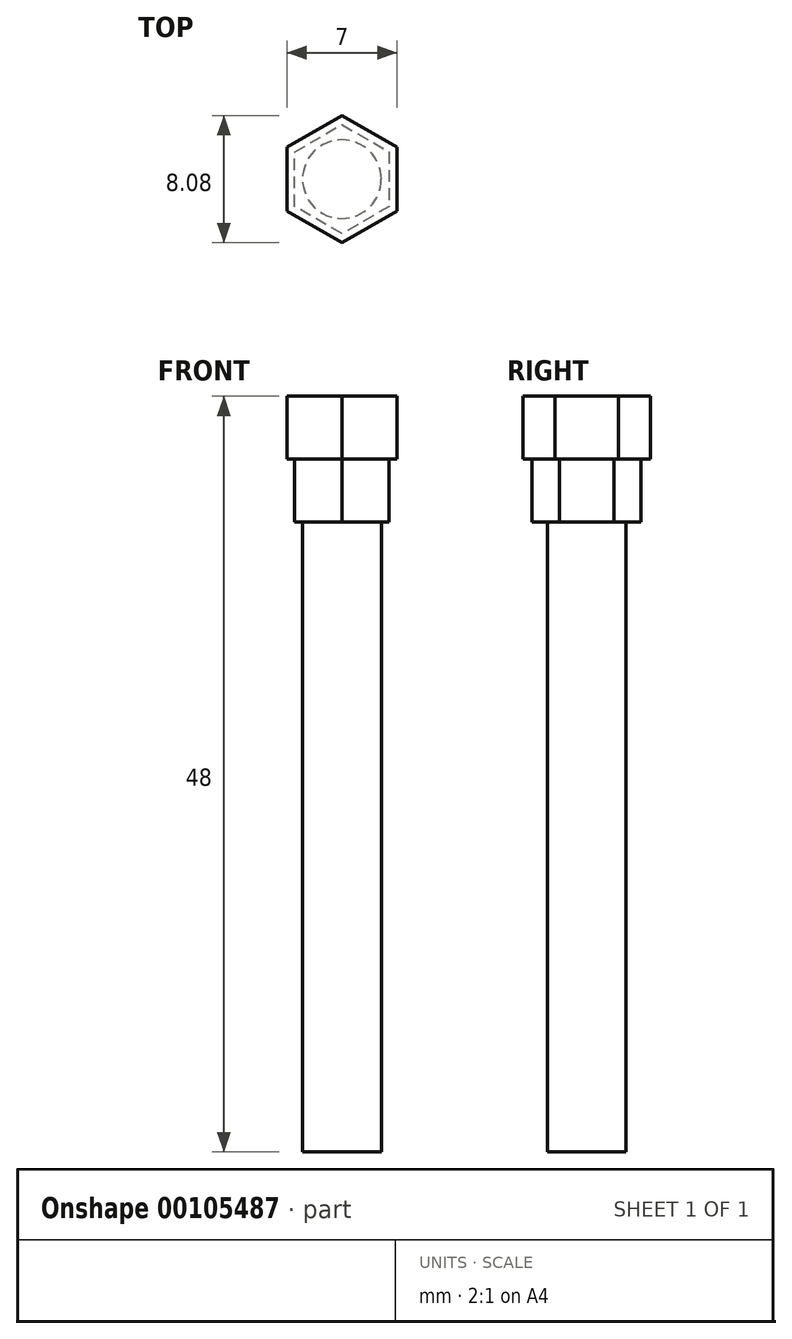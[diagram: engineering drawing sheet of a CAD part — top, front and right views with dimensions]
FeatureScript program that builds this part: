
annotation { "Feature Type Name" : "Feature", "Feature Type Description" : "" }
export const myFeature = defineFeature(function(context is Context, id is Id, definition is map)
    precondition{}
    {
        {
            var Q0;
            Q0=qCreatedBy(makeId("Top.planeOp"),FACE);
            var sketch = newSketch(context, id + "F0", { "sketchPlane" : qUnion([Q0])});
            skCircle(sketch, "E0", {"center": v(0, 0) * mm, "radius": 2.5 * mm});
            skSolve(sketch);
        }
        {
            var Q0;
            Q0=makeQuery(id+"F0.imprint","IMPRINT",FACE,{"disambiguationData":[TD([[makeQuery(id+"F0.imprint","IMPRINT",EDGE,{"derivedFrom":sQuery(id+"F0.wireOp",EDGE,"E0")}),1.0]])]});
            extrude(context, id + "F1", {"entities" : qUnion([Q0]), "depth" : 40 * mm});
        }
        {
            var Q0;
            Q0=makeQuery(id+"F1.opExtrude","CAP_FACE",FACE,{"disambiguationData":[OSD([sQuery(id+"F0.wireOp",EDGE,"E0")])],"isStart":false});
            var sketch = newSketch(context, id + "F2", { "sketchPlane" : qUnion([Q0])});
            skCircle(sketch, "E1.cCircle", {"center": v(0, 0) * mm, "radius": 3 * mm, "construction": true});
            skLineSegment(sketch, "E1.0", {"start": v(3, 1.73) * mm, "end": v(3, -1.73) * mm});
            skLineSegment(sketch, "E1.1", {"start": v(3, -1.73) * mm, "end": v(0, -3.46) * mm});
            skLineSegment(sketch, "E1.2", {"start": v(0, -3.46) * mm, "end": v(-3, -1.73) * mm});
            skLineSegment(sketch, "E1.3", {"start": v(-3, -1.73) * mm, "end": v(-3, 1.73) * mm});
            skLineSegment(sketch, "E1.4", {"start": v(-3, 1.73) * mm, "end": v(0, 3.46) * mm});
            skLineSegment(sketch, "E1.5", {"start": v(0, 3.46) * mm, "end": v(3, 1.73) * mm});
            skPoint(sketch, "E1.0.midPoint", {"position": v(3, 0) * mm});
            skSolve(sketch);
        }
        {
            var Q0;
            Q0=qSketchRegion(id+"F2",true);
            extrude(context, id + "F3", {"entities" : qUnion([Q0]), "operationType" : NewBodyOperationType.ADD, "depth" : 4 * mm});
        }
        {
            var Q0;
            Q0=makeQuery(id+"F3.opExtrude","CAP_FACE",FACE,{"disambiguationData":[OSD([sQuery(id+"F2.wireOp",EDGE,"E1.0"),sQuery(id+"F2.wireOp",EDGE,"E1.1"),sQuery(id+"F2.wireOp",EDGE,"E1.2"),sQuery(id+"F2.wireOp",EDGE,"E1.3"),sQuery(id+"F2.wireOp",EDGE,"E1.4"),sQuery(id+"F2.wireOp",EDGE,"E1.5")])],"isStart":false});
            var sketch = newSketch(context, id + "F4", { "sketchPlane" : qUnion([Q0])});
            skCircle(sketch, "E2.cCircle", {"center": v(0, 0) * mm, "radius": 3.5 * mm, "construction": true});
            skLineSegment(sketch, "E2.0", {"start": v(3.5, 2.02) * mm, "end": v(3.5, -2.02) * mm});
            skLineSegment(sketch, "E2.1", {"start": v(3.5, -2.02) * mm, "end": v(0, -4.04) * mm});
            skLineSegment(sketch, "E2.2", {"start": v(0, -4.04) * mm, "end": v(-3.5, -2.02) * mm});
            skLineSegment(sketch, "E2.3", {"start": v(-3.5, -2.02) * mm, "end": v(-3.5, 2.02) * mm});
            skLineSegment(sketch, "E2.4", {"start": v(-3.5, 2.02) * mm, "end": v(0, 4.04) * mm});
            skLineSegment(sketch, "E2.5", {"start": v(0, 4.04) * mm, "end": v(3.5, 2.02) * mm});
            skPoint(sketch, "E2.0.midPoint", {"position": v(3.5, 0) * mm});
            skSolve(sketch);
        }
        {
            var Q0;
            Q0=qSketchRegion(id+"F4",true);
            extrude(context, id + "F5", {"entities" : qUnion([Q0]), "operationType" : NewBodyOperationType.ADD, "depth" : 4 * mm});
        }
    });
